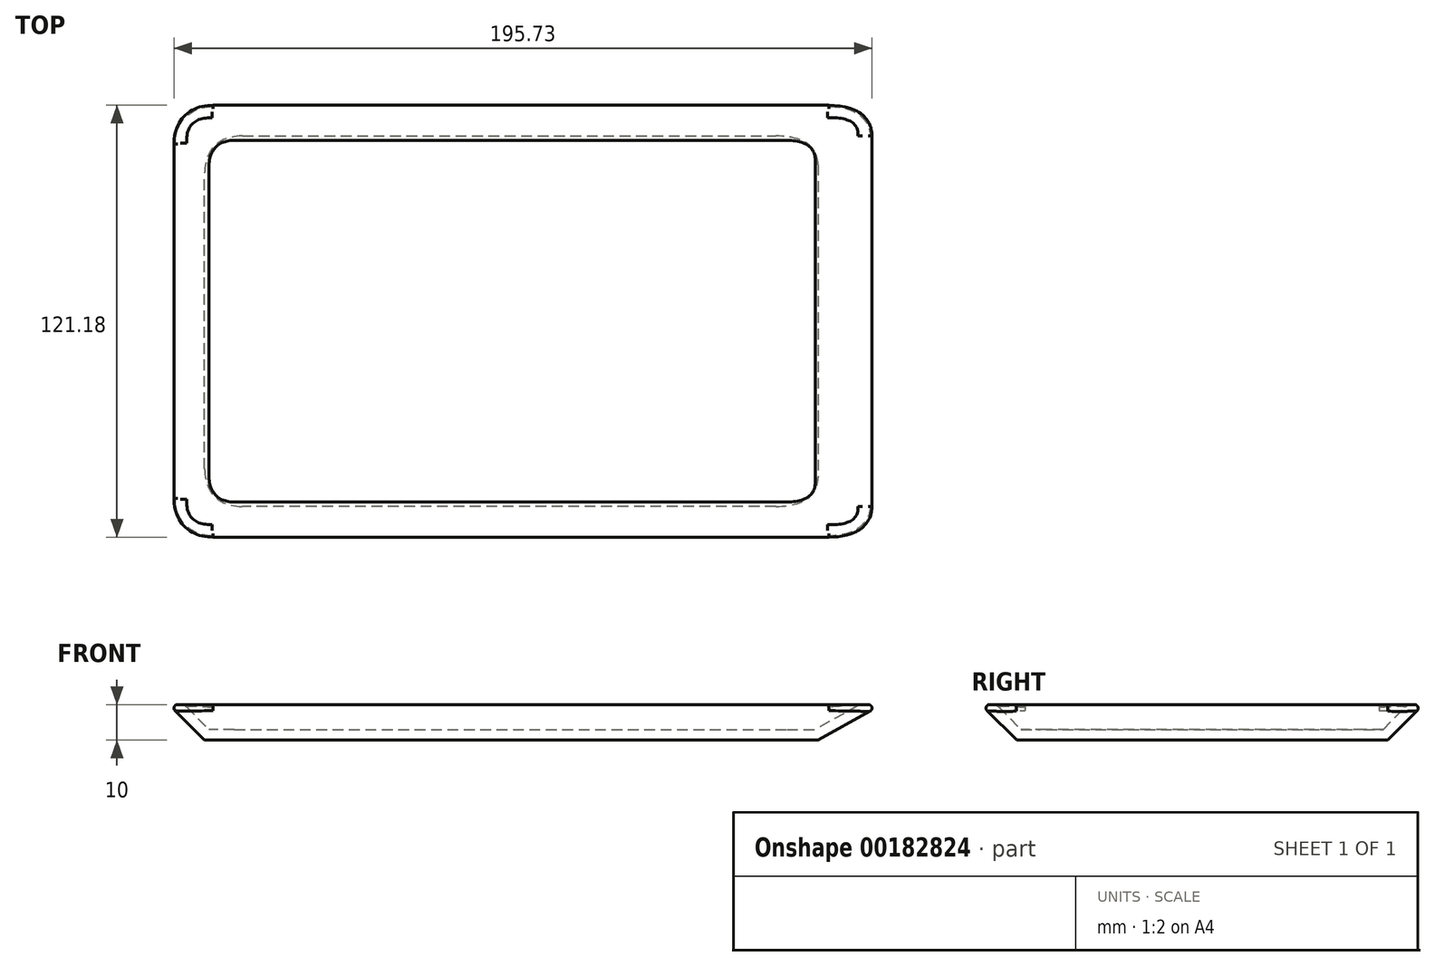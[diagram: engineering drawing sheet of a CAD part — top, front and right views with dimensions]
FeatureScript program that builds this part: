
annotation { "Feature Type Name" : "Feature", "Feature Type Description" : "" }
export const myFeature = defineFeature(function(context is Context, id is Id, definition is map)
    precondition{}
    {
        {
            var Q0;
            Q0=qCreatedBy(makeId("Top.planeOp"),FACE);
            var sketch = newSketch(context, id + "F0", { "sketchPlane" : qUnion([Q0])});
            skLineSegment(sketch, "E0", {"start": v(-100, 62) * mm, "end": v(100, 62) * mm});
            skLineSegment(sketch, "E1", {"start": v(100, 62) * mm, "end": v(100, -62) * mm});
            skLineSegment(sketch, "E2", {"start": v(100, -62) * mm, "end": v(-100, -62) * mm});
            skLineSegment(sketch, "E3", {"start": v(-100, -62) * mm, "end": v(-100, 62) * mm});
            skSolve(sketch);
        }
        {
            var Q0;
            Q0=makeQuery(id+"F0.imprint","IMPRINT",FACE,{"disambiguationData":[TD([[makeQuery(id+"F0.imprint","IMPRINT",EDGE,{"derivedFrom":sQuery(id+"F0.wireOp",EDGE,"E0")}),-1.0]])]});
            extrude(context, id + "F1", {"entities" : qUnion([Q0]), "depth" : 10 * mm});
        }
        {
            var Q0;
            Q0=makeQuery(id+"F1.opExtrude","CAP_EDGE",EDGE,{"disambiguationData":[OSD([sQuery(id+"F0.wireOp",EDGE,"E1")])],"isStart":true});
            chamfer(context, id + "F2", {"entities" : qUnion([Q0]), "chamferType" : ChamferType.TWO_OFFSETS, "width1" : 10 * mm, "oppositeDirection" : true, "width2" : 18 * mm, "tangentPropagation" : true});
        }
        {
            var Q0;
            Q0=makeQuery(id+"F1.opExtrude","CAP_EDGE",EDGE,{"disambiguationData":[OSD([sQuery(id+"F0.wireOp",EDGE,"E0")])],"isStart":true});
            var Q1;
            Q1=makeQuery(id+"F1.opExtrude","CAP_EDGE",EDGE,{"disambiguationData":[OSD([sQuery(id+"F0.wireOp",EDGE,"E3")])],"isStart":true});
            var Q2;
            Q2=makeQuery(id+"F1.opExtrude","CAP_EDGE",EDGE,{"disambiguationData":[OSD([sQuery(id+"F0.wireOp",EDGE,"E2")])],"isStart":true});
            chamfer(context, id + "F3", {"entities" : qUnion([Q0, Q1, Q2]), "width" : 10 * mm, "tangentPropagation" : true});
        }
        {
            var Q0;
            Q0=makeQuery(id+"F1.opExtrude","CAP_FACE",FACE,{"disambiguationData":[OSD([sQuery(id+"F0.wireOp",EDGE,"E0"),sQuery(id+"F0.wireOp",EDGE,"E1"),sQuery(id+"F0.wireOp",EDGE,"E2"),sQuery(id+"F0.wireOp",EDGE,"E3")])],"isStart":false});
            shell(context, id + "F4", {"entities" : qUnion([Q0]), "thickness" : 3 * mm});
        }
        {
            var Q0;
            Q0=makeQuery(id+"F3.opChamfer","BLEND_EDGE",EDGE,{"blendedFrom":[makeQuery(id+"F1.opExtrude","CAP_EDGE",EDGE,{"disambiguationData":[OSD([sQuery(id+"F0.wireOp",EDGE,"E2")])],"isStart":true}),makeQuery(id+"F2.opChamfer","BLEND_FACE",FACE,{"disambiguationData":[OSD([sQuery(id+"F0.wireOp",EDGE,"E1")])]})],"blendedInto":[makeQuery(id+"F2.opChamfer","BLEND_FACE",FACE,{"disambiguationData":[OSD([sQuery(id+"F0.wireOp",EDGE,"E1")])]})]});
            var Q1;
            Q1=makeQuery(id+"F3.opChamfer","BLEND_EDGE",EDGE,{"blendedFrom":[makeQuery(id+"F1.opExtrude","CAP_EDGE",EDGE,{"disambiguationData":[OSD([sQuery(id+"F0.wireOp",EDGE,"E0")])],"isStart":true}),makeQuery(id+"F2.opChamfer","BLEND_FACE",FACE,{"disambiguationData":[OSD([sQuery(id+"F0.wireOp",EDGE,"E1")])]})],"blendedInto":[makeQuery(id+"F2.opChamfer","BLEND_FACE",FACE,{"disambiguationData":[OSD([sQuery(id+"F0.wireOp",EDGE,"E1")])]})]});
            var Q2;
            Q2=makeQuery(id+"F3.opChamfer","BLEND_EDGE",EDGE,{"blendedFrom":[makeQuery(id+"F1.opExtrude","CAP_EDGE",EDGE,{"disambiguationData":[OSD([sQuery(id+"F0.wireOp",EDGE,"E3")])],"isStart":true}),makeQuery(id+"F1.opExtrude","CAP_EDGE",EDGE,{"disambiguationData":[OSD([sQuery(id+"F0.wireOp",EDGE,"E0")])],"isStart":true})],"blendedInto":[]});
            var Q3;
            Q3=makeQuery(id+"F3.opChamfer","BLEND_EDGE",EDGE,{"blendedFrom":[makeQuery(id+"F1.opExtrude","CAP_EDGE",EDGE,{"disambiguationData":[OSD([sQuery(id+"F0.wireOp",EDGE,"E3")])],"isStart":true}),makeQuery(id+"F1.opExtrude","CAP_EDGE",EDGE,{"disambiguationData":[OSD([sQuery(id+"F0.wireOp",EDGE,"E2")])],"isStart":true})],"blendedInto":[]});
            fillet(context, id + "F5", {"entities" : qUnion([Q0, Q1, Q2, Q3]), "radius" : 15 * mm, "tangentPropagation" : true, "allowEdgeOverflow" : false});
        }
        {
            var Q0;
            {var subQ0=sQuery(id+"F0.wireOp",EDGE,"E3");Q0=makeQuery(id+"F3.opChamfer","BLEND_EDGE",EDGE,{"blendedFrom":[makeQuery(id+"F1.opExtrude","CAP_EDGE",EDGE,{"disambiguationData":[OSD([subQ0])],"isStart":true}),makeQuery(id+"F1.opExtrude","CAP_FACE",FACE,{"disambiguationData":[OSD([sQuery(id+"F0.wireOp",EDGE,"E0"),sQuery(id+"F0.wireOp",EDGE,"E1"),sQuery(id+"F0.wireOp",EDGE,"E2"),subQ0])],"isStart":false})],"blendedInto":[makeQuery(id+"F1.opExtrude","CAP_FACE",FACE,{"disambiguationData":[OSD([sQuery(id+"F0.wireOp",EDGE,"E0"),sQuery(id+"F0.wireOp",EDGE,"E1"),sQuery(id+"F0.wireOp",EDGE,"E2"),subQ0])],"isStart":false})]});}
            fillet(context, id + "F6", {"entities" : qUnion([Q0]), "radius" : 1 * mm, "tangentPropagation" : true, "allowEdgeOverflow" : false});
        }
        {
            var Q0;
            Q0=makeQuery(id+"F4.opShell","OFFSET_EDGE",EDGE,{"disambiguationData":[OSD([sQuery(id+"F0.wireOp",EDGE,"E0"),sQuery(id+"F0.wireOp",EDGE,"E1")])]});
            var Q1;
            Q1=makeQuery(id+"F4.opShell","OFFSET_EDGE",EDGE,{"disambiguationData":[OSD([sQuery(id+"F0.wireOp",EDGE,"E1"),sQuery(id+"F0.wireOp",EDGE,"E2")])]});
            var Q2;
            Q2=makeQuery(id+"F4.opShell","OFFSET_EDGE",EDGE,{"disambiguationData":[OSD([sQuery(id+"F0.wireOp",EDGE,"E2"),sQuery(id+"F0.wireOp",EDGE,"E3")])]});
            var Q3;
            Q3=makeQuery(id+"F4.opShell","OFFSET_EDGE",EDGE,{"disambiguationData":[OSD([sQuery(id+"F0.wireOp",EDGE,"E0"),sQuery(id+"F0.wireOp",EDGE,"E3")])]});
            fillet(context, id + "F7", {"entities" : qUnion([Q0, Q1, Q2, Q3]), "radius" : 10 * mm, "tangentPropagation" : true, "allowEdgeOverflow" : false});
        }
        {
            var Q0;
            {var subQ0=sQuery(id+"F0.wireOp",EDGE,"E3");var subQ1=sQuery(id+"F0.wireOp",EDGE,"E2");var subQ2=sQuery(id+"F0.wireOp",EDGE,"E1");var subQ3=sQuery(id+"F0.wireOp",EDGE,"E0");Q0=makeQuery(id+"F4.opShell","OFFSET_EDGE",EDGE,{"disambiguationData":[OSD([subQ3,subQ2,subQ1,subQ0]),TDD([makeQuery(id+"F3.opChamfer","BLEND_EDGE",EDGE,{"blendedFrom":[makeQuery(id+"F1.opExtrude","CAP_EDGE",EDGE,{"disambiguationData":[OSD([subQ3])],"isStart":true}),makeQuery(id+"F1.opExtrude","CAP_FACE",FACE,{"disambiguationData":[OSD([subQ3,subQ2,subQ1,subQ0])],"isStart":false})],"blendedInto":[makeQuery(id+"F1.opExtrude","CAP_FACE",FACE,{"disambiguationData":[OSD([subQ3,subQ2,subQ1,subQ0])],"isStart":false})]})])]});}
            fillet(context, id + "F8", {"entities" : qUnion([Q0]), "radius" : 2.5 * mm, "tangentPropagation" : true, "allowEdgeOverflow" : false});
        }
    });
